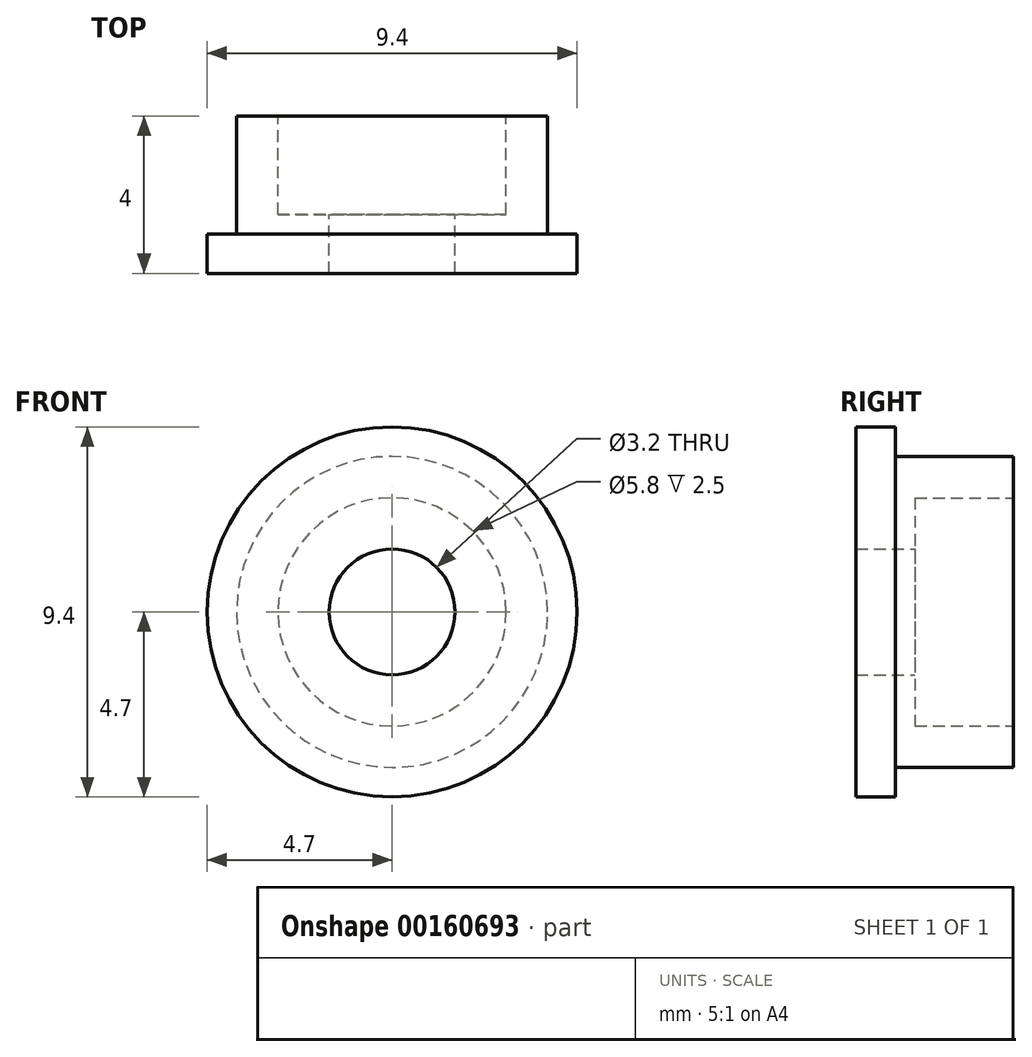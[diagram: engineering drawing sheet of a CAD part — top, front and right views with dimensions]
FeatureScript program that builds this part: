
annotation { "Feature Type Name" : "Feature", "Feature Type Description" : "" }
export const myFeature = defineFeature(function(context is Context, id is Id, definition is map)
    precondition{}
    {
        {
            var Q0;
            Q0=qCreatedBy(makeId("Right.planeOp"),FACE);
            var sketch = newSketch(context, id + "F0", { "sketchPlane" : qUnion([Q0])});
            skLineSegment(sketch, "E0", {"start": v(11.47, 0) * mm, "end": v(0, 0) * mm, "construction": true});
            skLineSegment(sketch, "E1", {"start": v(1.5, 1.6) * mm, "end": v(0, 1.6) * mm});
            skLineSegment(sketch, "E2", {"start": v(1.5, 1.6) * mm, "end": v(1.5, 2.9) * mm});
            skLineSegment(sketch, "E3", {"start": v(4, 2.9) * mm, "end": v(1.5, 2.9) * mm});
            skLineSegment(sketch, "E4", {"start": v(4, 2.9) * mm, "end": v(4, 3.95) * mm});
            skLineSegment(sketch, "E5", {"start": v(1, 3.95) * mm, "end": v(4, 3.95) * mm});
            skLineSegment(sketch, "E6", {"start": v(1, 3.95) * mm, "end": v(1, 4.7) * mm});
            skLineSegment(sketch, "E7", {"start": v(0, 4.7) * mm, "end": v(1, 4.7) * mm});
            skLineSegment(sketch, "E8", {"start": v(0, 4.7) * mm, "end": v(0, 1.6) * mm});
            skSolve(sketch);
        }
        {
            var Q0;
            Q0=makeQuery(id+"F0.imprint","IMPRINT",FACE,{"disambiguationData":[TD([[makeQuery(id+"F0.imprint","IMPRINT",EDGE,{"derivedFrom":sQuery(id+"F0.wireOp",EDGE,"E1")}),-1.0]])]});
            var Q1;
            Q1=sQuery(id+"F0.wireOp",EDGE,"E0");
            revolve(context, id + "F1", {"entities" : qUnion([Q0]), "axis" : qUnion([Q1]), "revolveType" : RevolveType.FULL});
        }
    });
